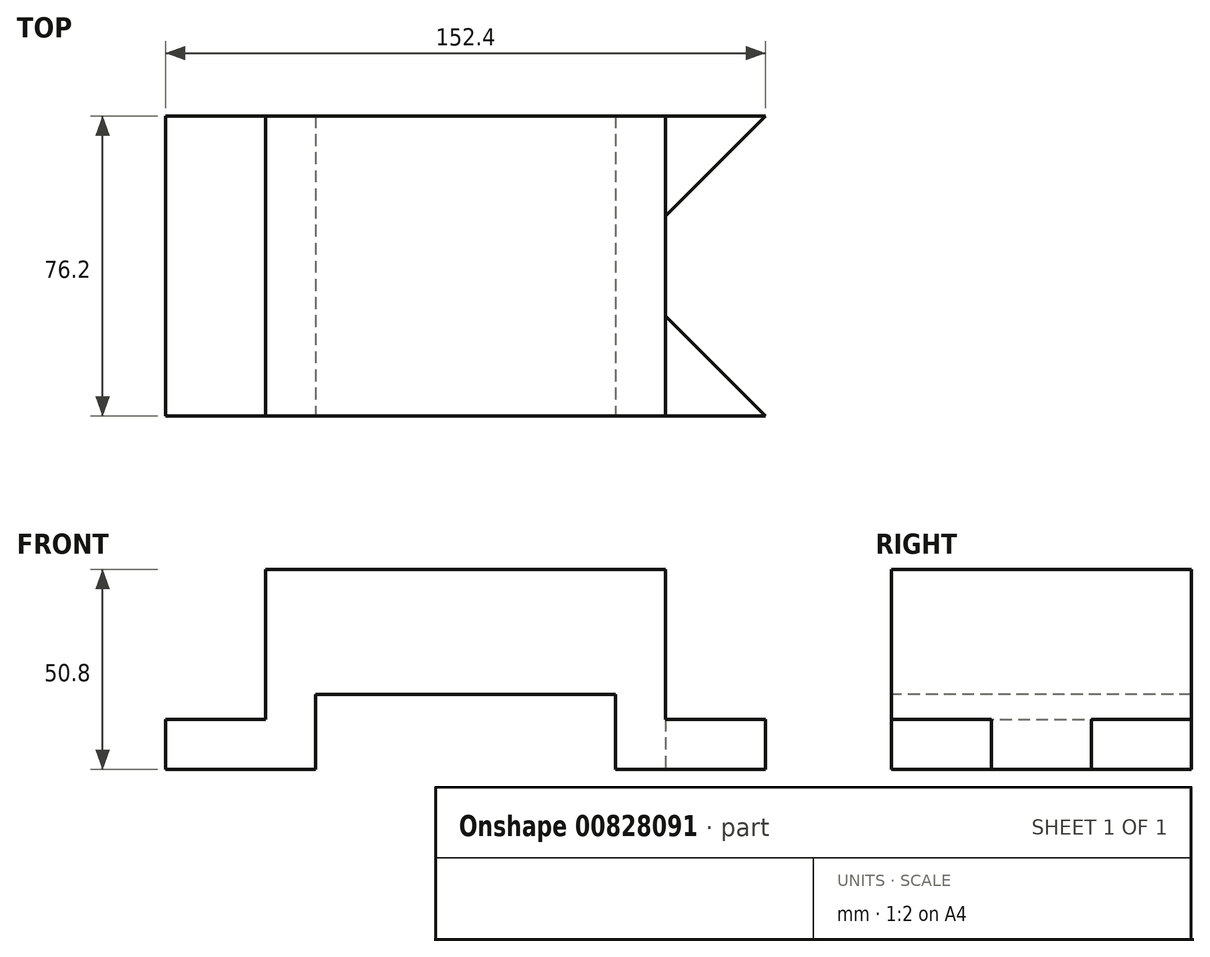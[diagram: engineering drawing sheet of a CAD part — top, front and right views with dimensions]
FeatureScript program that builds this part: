
annotation { "Feature Type Name" : "Feature", "Feature Type Description" : "" }
export const myFeature = defineFeature(function(context is Context, id is Id, definition is map)
    precondition{}
    {
        {
            var Q0;
            Q0=qCreatedBy(makeId("Top.planeOp"),FACE);
            var sketch = newSketch(context, id + "F0", { "sketchPlane" : qUnion([Q0])});
            skLineSegment(sketch, "E0.bottom", {"start": v(-45.16, 51.45) * mm, "end": v(56.44, 51.45) * mm});
            skLineSegment(sketch, "E0.top", {"start": v(-45.16, -24.75) * mm, "end": v(56.44, -24.75) * mm});
            skLineSegment(sketch, "E0.left", {"start": v(-45.16, 51.45) * mm, "end": v(-45.16, -24.75) * mm});
            skLineSegment(sketch, "E0.right", {"start": v(56.44, 51.45) * mm, "end": v(56.44, -24.75) * mm});
            skLineSegment(sketch, "E1", {"start": v(-45.16, -24.75) * mm, "end": v(-70.56, -24.75) * mm});
            skLineSegment(sketch, "E2", {"start": v(-70.56, -24.75) * mm, "end": v(-70.56, 51.45) * mm});
            skLineSegment(sketch, "E3", {"start": v(-70.56, 51.45) * mm, "end": v(-45.16, 51.45) * mm});
            skLineSegment(sketch, "E4", {"start": v(56.44, -24.75) * mm, "end": v(81.84, -24.75) * mm});
            skLineSegment(sketch, "E5", {"start": v(81.84, -24.75) * mm, "end": v(56.44, 0.65) * mm});
            skLineSegment(sketch, "E6", {"start": v(56.44, 0.65) * mm, "end": v(56.44, 26.05) * mm});
            skLineSegment(sketch, "E7", {"start": v(56.44, 26.05) * mm, "end": v(81.84, 51.45) * mm});
            skLineSegment(sketch, "E8", {"start": v(81.84, 51.45) * mm, "end": v(56.44, 51.45) * mm});
            skSolve(sketch);
        }
        {
            var Q0;
            Q0=makeQuery(id+"F0.imprint","IMPRINT",FACE,{"disambiguationData":[TD([[makeQuery(id+"F0.imprint","IMPRINT",EDGE,{"derivedFrom":sQuery(id+"F0.wireOp",EDGE,"E0.left")}),-1.0]])]});
            extrude(context, id + "F1", {"entities" : qUnion([Q0]), "depth" : 12.7 * mm, "offsetDistance" : 25.4 * mm});
        }
        {
            var Q0;
            {var subQ1=sQuery(id+"F0.wireOp",EDGE,"E0.bottom");Q0=makeQuery(id+"F0.imprint","IMPRINT",FACE,{"disambiguationData":[TD([[makeQuery(id+"F0.imprint","IMPRINT",EDGE,{"derivedFrom":subQ1}),-1.0]])]});}
            extrude(context, id + "F2", {"entities" : qUnion([Q0]), "operationType" : NewBodyOperationType.ADD, "depth" : 50.8 * mm, "offsetDistance" : 25.4 * mm});
        }
        {
            var Q0;
            {var subQ2=sQuery(id+"F0.wireOp",EDGE,"E7");Q0=makeQuery(id+"F0.imprint","IMPRINT",FACE,{"disambiguationData":[TD([[makeQuery(id+"F0.imprint","IMPRINT",EDGE,{"derivedFrom":subQ2}),1.0]])]});}
            extrude(context, id + "F3", {"entities" : qUnion([Q0]), "operationType" : NewBodyOperationType.ADD, "depth" : 12.7 * mm, "offsetDistance" : 25.4 * mm});
        }
        {
            var Q0;
            {var subQ0=sQuery(id+"F0.wireOp",EDGE,"E4");Q0=makeQuery(id+"F0.imprint","IMPRINT",FACE,{"disambiguationData":[TD([[makeQuery(id+"F0.imprint","IMPRINT",EDGE,{"derivedFrom":subQ0}),1.0]])]});}
            extrude(context, id + "F4", {"entities" : qUnion([Q0]), "operationType" : NewBodyOperationType.ADD, "depth" : 12.7 * mm, "offsetDistance" : 25.4 * mm});
        }
        {
            var Q0;
            Q0=makeQuery(id+"F4.boolean.opBoolean","MERGE",FACE,{"derivedFrom":[makeQuery(id+"F2.boolean.opBoolean","MERGE",FACE,{"derivedFrom":[makeQuery(id+"F1.opExtrude","SWEPT_FACE",FACE,{"disambiguationData":[OSD([sQuery(id+"F0.wireOp",EDGE,"E1")])]}),makeQuery(id+"F2.opExtrude","SWEPT_FACE",FACE,{"disambiguationData":[OSD([sQuery(id+"F0.wireOp",EDGE,"E0.top")])]})]}),makeQuery(id+"F4.opExtrude","SWEPT_FACE",FACE,{"disambiguationData":[OSD([sQuery(id+"F0.wireOp",EDGE,"E4")])]})]});
            var sketch = newSketch(context, id + "F5", { "sketchPlane" : qUnion([Q0])});
            skLineSegment(sketch, "E9", {"start": v(-32.46, 0) * mm, "end": v(-32.46, 19.05) * mm});
            skLineSegment(sketch, "E10", {"start": v(-32.46, 19.05) * mm, "end": v(43.74, 19.05) * mm});
            skLineSegment(sketch, "E11", {"start": v(43.74, 19.05) * mm, "end": v(43.74, 0) * mm});
            skSolve(sketch);
        }
        {
            var Q0;
            {var subQ0=sQuery(id+"F5.wireOp",EDGE,"E9");Q0=makeQuery(id+"F5.imprint","IMPRINT",FACE,{"disambiguationData":[TD([[makeQuery(id+"F5.imprint","IMPRINT",EDGE,{"derivedFrom":subQ0}),-1.0]])]});}
            extrude(context, id + "F6", {"entities" : qUnion([Q0]), "operationType" : NewBodyOperationType.REMOVE, "endBound" : BoundingType.THROUGH_ALL, "oppositeDirection" : true, "depth" : 25.4 * mm, "offsetDistance" : 25.4 * mm});
        }
    });
